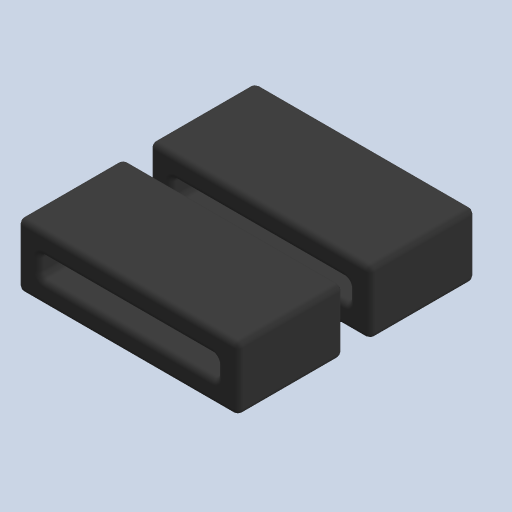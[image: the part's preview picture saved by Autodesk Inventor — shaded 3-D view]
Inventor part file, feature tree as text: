
AUTODESK INVENTOR PART (.ipt)
format: ipt  version: 2023 (Build 270158000, 158)  size: 587,264 bytes
history: native  units: mm
features: other x10, extrude x5, fillet x4, pattern_linear x1
ambient origin geometry x8: Origin, YZ Plane, XZ Plane, XY Plane, X Axis, Y Axis, Z Axis, Center Point
bodies: Solid1 (feature_tree)
feature tree (20):
  other  "NP2_Payload.ipt"
  other  "Sk:Base"
  other  "Sk:Params"
  extrude  "Ex:Base"  Depth=10.0mm
  extrude  "Ex:EndLip"  Depth=0.8mm TaperAngle=0.0deg
  other  "EndPlane"
  other  "Sk:Slot"
  extrude  "Ex:Slot1"  Depth=0.8mm TaperAngle=0.0deg
  extrude  "Ex:SlotEnd"  Depth=4.0mm TaperAngle=0.0deg
  fillet  "Fillet:Slot"  Radius=0.8mm
  other  "Sk:TaperSection"
  pattern_linear  "Pat:Slot2"  Spacing1=0.02mm  [1 undecoded]
  extrude  "Ex:TaperSection"  Depth=2.0mm
  fillet  "Fillet:ExcludeLine1"  Radius=0.2mm
  fillet  "Fillet:Final1"  Radius=20.0mm
  fillet  "Fillet:Final2"  Radius=0.2mm
  other  "TaggingFeature1"
  other  "Sk:EndLip"
  other  "Solid1::NP2_Payload.ipt"
  other  "Srf1"
note: 1 required parameter value undecoded (feature->parameter linkage not recoverable at this tier; creation-order binding heuristic only, values carry confidence <= 0.55)
